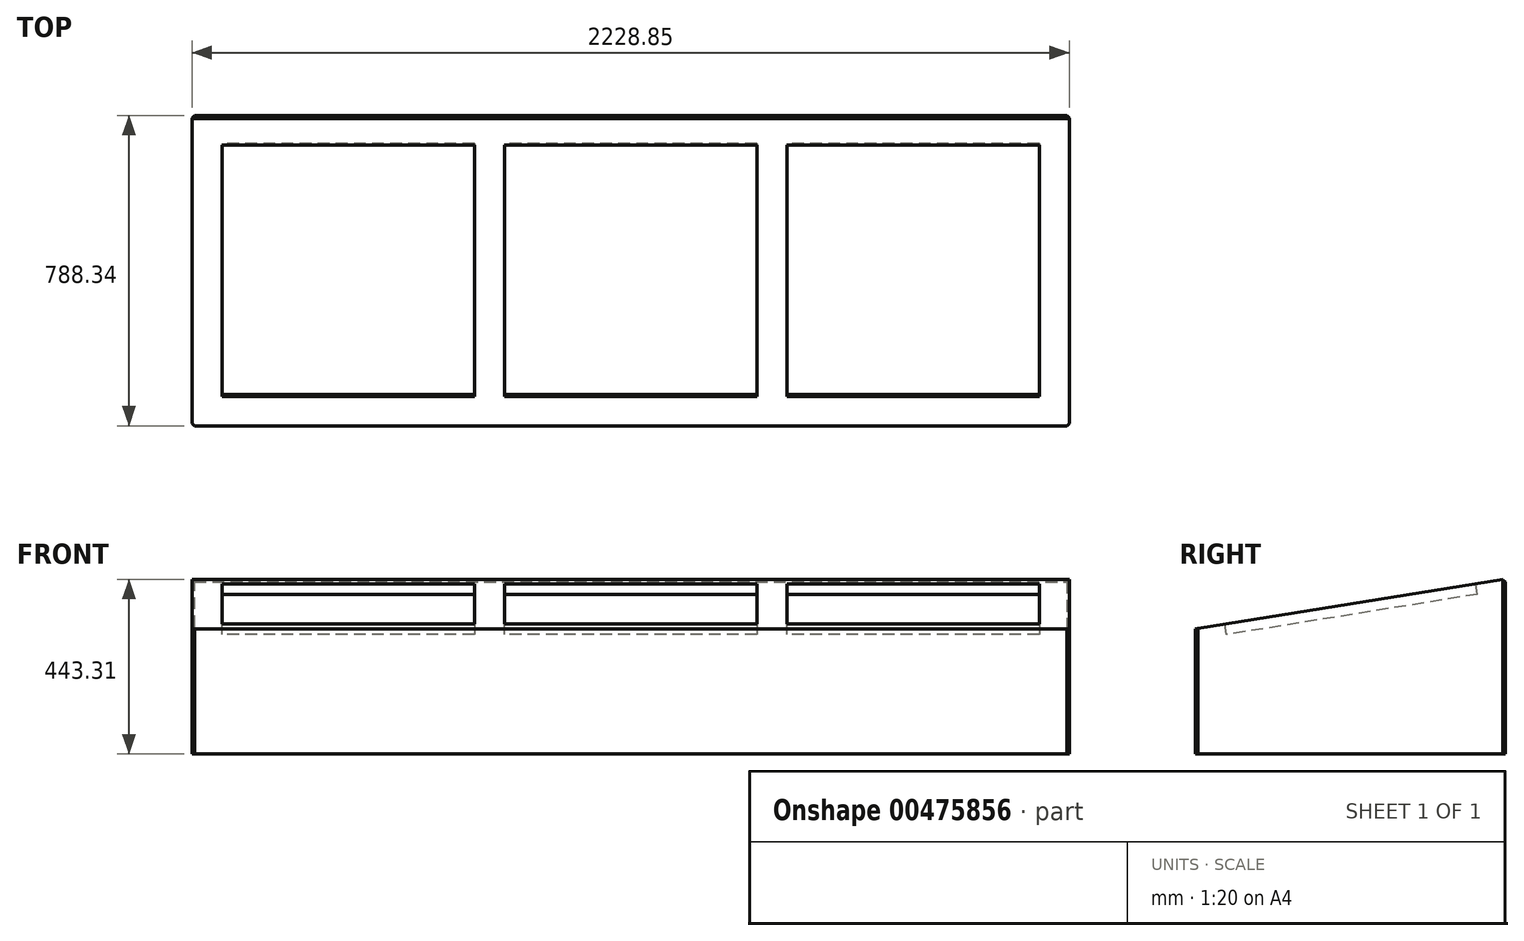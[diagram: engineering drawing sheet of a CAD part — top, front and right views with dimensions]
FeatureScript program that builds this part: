
annotation { "Feature Type Name" : "Feature", "Feature Type Description" : "" }
export const myFeature = defineFeature(function(context is Context, id is Id, definition is map)
    precondition{}
    {
        {
            var Q0;
            Q0=qCreatedBy(makeId("Top.planeOp"),FACE);
            var sketch = newSketch(context, id + "F0", { "sketchPlane" : qUnion([Q0])});
            skLineSegment(sketch, "E0.bottom", {"start": v(1114.42, -394.17) * mm, "end": v(-1114.42, -394.17) * mm});
            skLineSegment(sketch, "E0.top", {"start": v(1114.42, 394.17) * mm, "end": v(-1114.42, 394.17) * mm});
            skLineSegment(sketch, "E0.left", {"start": v(1114.42, -394.17) * mm, "end": v(1114.42, 394.17) * mm});
            skLineSegment(sketch, "E0.right", {"start": v(-1114.42, -394.17) * mm, "end": v(-1114.42, 394.17) * mm});
            skPoint(sketch, "E0.middle", {"position": v(0, 0) * mm});
            skSolve(sketch);
        }
        {
            var Q0;
            Q0=makeQuery(id+"F0.imprint","IMPRINT",FACE,{"disambiguationData":[TD([[makeQuery(id+"F0.imprint","IMPRINT",EDGE,{"derivedFrom":sQuery(id+"F0.wireOp",EDGE,"E0.bottom")}),-1.0]])]});
            extrude(context, id + "F1", {"entities" : qUnion([Q0]), "depth" : 444.5 * mm});
        }
        {
            var Q0;
            Q0=makeQuery(id+"F1.opExtrude","SWEPT_FACE",FACE,{"disambiguationData":[OSD([sQuery(id+"F0.wireOp",EDGE,"E0.right")])]});
            var sketch = newSketch(context, id + "F2", { "sketchPlane" : qUnion([Q0])});
            skLineSegment(sketch, "E1", {"start": v(394.17, 444.5) * mm, "end": v(394.17, 317.5) * mm});
            skLineSegment(sketch, "E2", {"start": v(394.17, 317.5) * mm, "end": v(-394.17, 444.5) * mm});
            skLineSegment(sketch, "E3", {"start": v(-394.17, 444.5) * mm, "end": v(394.17, 444.5) * mm});
            skSolve(sketch);
        }
        {
            var Q0;
            Q0=makeQuery(id+"F2.imprint","IMPRINT",FACE,{"disambiguationData":[TD([[makeQuery(id+"F2.imprint","IMPRINT",EDGE,{"derivedFrom":sQuery(id+"F2.wireOp",EDGE,"E1")}),-1.0]])]});
            extrude(context, id + "F3", {"entities" : qUnion([Q0]), "operationType" : NewBodyOperationType.REMOVE, "oppositeDirection" : true, "depth" : 2228.85 * mm});
        }
        {
            var Q0;
            Q0=makeQuery(id+"F3.boolean.opBoolean","COPY",FACE,{"derivedFrom":makeQuery(id+"F3.opExtrude","SWEPT_FACE",FACE,{"disambiguationData":[OSD([sQuery(id+"F2.wireOp",EDGE,"E2")])]})});
            var sketch = newSketch(context, id + "F4", { "sketchPlane" : qUnion([Q0])});
            skLineSegment(sketch, "E4", {"start": v(1114.42, -338.66) * mm, "end": v(1114.42, 459.85) * mm});
            skLineSegment(sketch, "E5", {"start": v(1114.43, 459.85) * mm, "end": v(-1114.43, 459.85) * mm});
            skLineSegment(sketch, "E6", {"start": v(-1114.42, 459.85) * mm, "end": v(-1114.42, -338.66) * mm});
            skLineSegment(sketch, "E7", {"start": v(-1114.43, -338.66) * mm, "end": v(1114.43, -338.66) * mm});
            skPoint(sketch, "E8.endSnap0", {"position": v(1114.42, 60.6) * mm});
            skPoint(sketch, "E9", {"position": v(-717.55, 60.6) * mm});
            skPoint(sketch, "E10", {"position": v(717.55, 60.6) * mm});
            skLineSegment(sketch, "E11", {"start": v(320.68, 60.6) * mm, "end": v(320.68, 383.65) * mm});
            skLineSegment(sketch, "E12", {"start": v(-396.87, 60.6) * mm, "end": v(-396.87, 383.65) * mm});
            skLineSegment(sketch, "E13", {"start": v(1038.23, 60.6) * mm, "end": v(1038.23, 383.65) * mm});
            skPoint(sketch, "E14.middle", {"position": v(0, 60.6) * mm});
            skLineSegment(sketch, "E15.bottom", {"start": v(1038.23, 383.65) * mm, "end": v(396.88, 383.65) * mm});
            skLineSegment(sketch, "E15.top", {"start": v(1038.23, -262.46) * mm, "end": v(396.88, -262.46) * mm});
            skLineSegment(sketch, "E15.left", {"start": v(1038.23, 383.65) * mm, "end": v(1038.23, -262.46) * mm});
            skLineSegment(sketch, "E15.right", {"start": v(396.88, 383.65) * mm, "end": v(396.88, -262.46) * mm});
            skLineSegment(sketch, "E16.bottom", {"start": v(320.68, 383.65) * mm, "end": v(-320.67, 383.65) * mm});
            skLineSegment(sketch, "E16.top", {"start": v(320.68, -262.46) * mm, "end": v(-320.67, -262.46) * mm});
            skLineSegment(sketch, "E16.left", {"start": v(320.68, 383.65) * mm, "end": v(320.68, -262.46) * mm});
            skLineSegment(sketch, "E16.right", {"start": v(-320.67, 383.65) * mm, "end": v(-320.67, -262.46) * mm});
            skLineSegment(sketch, "E17.bottom", {"start": v(-396.87, 383.65) * mm, "end": v(-1038.22, 383.65) * mm});
            skLineSegment(sketch, "E17.top", {"start": v(-396.87, -262.46) * mm, "end": v(-1038.22, -262.46) * mm});
            skLineSegment(sketch, "E17.left", {"start": v(-396.87, 383.65) * mm, "end": v(-396.87, -262.46) * mm});
            skLineSegment(sketch, "E17.right", {"start": v(-1038.22, 383.65) * mm, "end": v(-1038.22, -262.46) * mm});
            skSolve(sketch);
        }
        {
            var Q0;
            {var subQ3=sQuery(id+"F4.wireOp",EDGE,"E16.bottom");Q0=makeQuery(id+"F4.imprint","IMPRINT",FACE,{"disambiguationData":[TD([[makeQuery(id+"F4.imprint","IMPRINT",EDGE,{"derivedFrom":subQ3}),1.0]])]});}
            var Q1;
            {var subQ3=sQuery(id+"F4.wireOp",EDGE,"E17.bottom");Q1=makeQuery(id+"F4.imprint","IMPRINT",FACE,{"disambiguationData":[TD([[makeQuery(id+"F4.imprint","IMPRINT",EDGE,{"derivedFrom":subQ3}),1.0]])]});}
            var Q2;
            {var subQ3=sQuery(id+"F4.wireOp",EDGE,"E15.bottom");Q2=makeQuery(id+"F4.imprint","IMPRINT",FACE,{"disambiguationData":[TD([[makeQuery(id+"F4.imprint","IMPRINT",EDGE,{"derivedFrom":subQ3}),1.0]])]});}
            extrude(context, id + "F5", {"entities" : qUnion([Q0, Q1, Q2]), "operationType" : NewBodyOperationType.REMOVE, "oppositeDirection" : true, "depth" : 27.01 * mm});
        }
        {
            var Q0;
            Q0=makeQuery(id+"F5.boolean.opBoolean","COPY",EDGE,{"derivedFrom":makeQuery(id+"F5.opExtrude","CAP_EDGE",EDGE,{"disambiguationData":[OSD([sQuery(id+"F4.wireOp",EDGE,"E15.right")])],"isStart":true})});
            var Q1;
            Q1=makeQuery(id+"F5.boolean.opBoolean","COPY",EDGE,{"derivedFrom":makeQuery(id+"F5.opExtrude","CAP_EDGE",EDGE,{"disambiguationData":[OSD([sQuery(id+"F4.wireOp",EDGE,"E16.left")])],"isStart":true})});
            var Q2;
            Q2=makeQuery(id+"F5.boolean.opBoolean","COPY",EDGE,{"derivedFrom":makeQuery(id+"F5.opExtrude","CAP_EDGE",EDGE,{"disambiguationData":[OSD([sQuery(id+"F4.wireOp",EDGE,"E16.right")])],"isStart":true})});
            var Q3;
            Q3=makeQuery(id+"F5.boolean.opBoolean","COPY",EDGE,{"derivedFrom":makeQuery(id+"F5.opExtrude","CAP_EDGE",EDGE,{"disambiguationData":[OSD([sQuery(id+"F4.wireOp",EDGE,"E17.left")])],"isStart":true})});
            var Q4;
            Q4=makeQuery(id+"F5.boolean.opBoolean","COPY",EDGE,{"derivedFrom":makeQuery(id+"F5.opExtrude","CAP_EDGE",EDGE,{"disambiguationData":[OSD([sQuery(id+"F4.wireOp",EDGE,"E17.right")])],"isStart":true})});
            var Q5;
            Q5=makeQuery(id+"F5.boolean.opBoolean","COPY",EDGE,{"derivedFrom":makeQuery(id+"F5.opExtrude","CAP_EDGE",EDGE,{"disambiguationData":[OSD([sQuery(id+"F4.wireOp",EDGE,"E17.bottom")])],"isStart":true})});
            var Q6;
            Q6=makeQuery(id+"F5.boolean.opBoolean","COPY",EDGE,{"derivedFrom":makeQuery(id+"F5.opExtrude","CAP_EDGE",EDGE,{"disambiguationData":[OSD([sQuery(id+"F4.wireOp",EDGE,"E17.top")])],"isStart":true})});
            var Q7;
            Q7=makeQuery(id+"F5.boolean.opBoolean","COPY",EDGE,{"derivedFrom":makeQuery(id+"F5.opExtrude","CAP_EDGE",EDGE,{"disambiguationData":[OSD([sQuery(id+"F4.wireOp",EDGE,"E16.bottom")])],"isStart":true})});
            var Q8;
            Q8=makeQuery(id+"F5.boolean.opBoolean","COPY",EDGE,{"derivedFrom":makeQuery(id+"F5.opExtrude","CAP_EDGE",EDGE,{"disambiguationData":[OSD([sQuery(id+"F4.wireOp",EDGE,"E16.top")])],"isStart":true})});
            var Q9;
            Q9=makeQuery(id+"F5.boolean.opBoolean","COPY",EDGE,{"derivedFrom":makeQuery(id+"F5.opExtrude","CAP_EDGE",EDGE,{"disambiguationData":[OSD([sQuery(id+"F4.wireOp",EDGE,"E15.top")])],"isStart":true})});
            var Q10;
            Q10=makeQuery(id+"F5.boolean.opBoolean","COPY",EDGE,{"derivedFrom":makeQuery(id+"F5.opExtrude","CAP_EDGE",EDGE,{"disambiguationData":[OSD([sQuery(id+"F4.wireOp",EDGE,"E15.left")])],"isStart":true})});
            var Q11;
            Q11=makeQuery(id+"F5.boolean.opBoolean","COPY",EDGE,{"derivedFrom":makeQuery(id+"F5.opExtrude","CAP_EDGE",EDGE,{"disambiguationData":[OSD([sQuery(id+"F4.wireOp",EDGE,"E15.bottom")])],"isStart":true})});
            var Q12;
            {var subQ0=sQuery(id+"F0.wireOp",EDGE,"E0.top");Q12=makeQuery(id+"F3.boolean.opBoolean","MERGE",EDGE,{"derivedFrom":[makeQuery(id+"F1.opExtrude","CAP_EDGE",EDGE,{"disambiguationData":[OSD([subQ0])],"isStart":false}),makeQuery(id+"F3.opExtrude","SWEPT_EDGE",EDGE,{"disambiguationData":[OSD([subQ0,sQuery(id+"F0.wireOp",EDGE,"E0.right"),sQuery(id+"F2.wireOp",EDGE,"E2"),sQuery(id+"F2.wireOp",EDGE,"E3")])]})]});}
            var Q13;
            Q13=makeQuery(id+"F3.boolean.opBoolean","COPY",EDGE,{"derivedFrom":makeQuery(id+"F3.opExtrude","CAP_EDGE",EDGE,{"disambiguationData":[OSD([sQuery(id+"F2.wireOp",EDGE,"E2")])],"isStart":false})});
            var Q14;
            Q14=makeQuery(id+"F3.boolean.opBoolean","COPY",EDGE,{"derivedFrom":makeQuery(id+"F3.opExtrude","SWEPT_EDGE",EDGE,{"disambiguationData":[OSD([sQuery(id+"F0.wireOp",EDGE,"E0.bottom"),sQuery(id+"F0.wireOp",EDGE,"E0.right"),sQuery(id+"F2.wireOp",EDGE,"E1"),sQuery(id+"F2.wireOp",EDGE,"E2")])]})});
            var Q15;
            Q15=makeQuery(id+"F3.boolean.opBoolean","COPY",EDGE,{"derivedFrom":makeQuery(id+"F3.opExtrude","CAP_EDGE",EDGE,{"disambiguationData":[OSD([sQuery(id+"F2.wireOp",EDGE,"E2")])],"isStart":true})});
            var Q16;
            Q16=makeQuery(id+"F1.opExtrude","SWEPT_EDGE",EDGE,{"disambiguationData":[OSD([sQuery(id+"F0.wireOp",EDGE,"E0.top"),sQuery(id+"F0.wireOp",EDGE,"E0.right")])]});
            var Q17;
            Q17=makeQuery(id+"F1.opExtrude","SWEPT_EDGE",EDGE,{"disambiguationData":[OSD([sQuery(id+"F0.wireOp",EDGE,"E0.bottom"),sQuery(id+"F0.wireOp",EDGE,"E0.right")])]});
            var Q18;
            Q18=makeQuery(id+"F1.opExtrude","SWEPT_EDGE",EDGE,{"disambiguationData":[OSD([sQuery(id+"F0.wireOp",EDGE,"E0.bottom"),sQuery(id+"F0.wireOp",EDGE,"E0.left")])]});
            var Q19;
            Q19=makeQuery(id+"F1.opExtrude","SWEPT_EDGE",EDGE,{"disambiguationData":[OSD([sQuery(id+"F0.wireOp",EDGE,"E0.top"),sQuery(id+"F0.wireOp",EDGE,"E0.left")])]});
            chamfer(context, id + "F6", {"entities" : qUnion([Q0, Q1, Q2, Q3, Q4, Q5, Q6, Q7, Q8, Q9, Q10, Q11, Q12, Q13, Q14, Q15, Q16, Q17, Q18, Q19]), "width" : 6.35 * mm, "tangentPropagation" : true});
        }
    });
